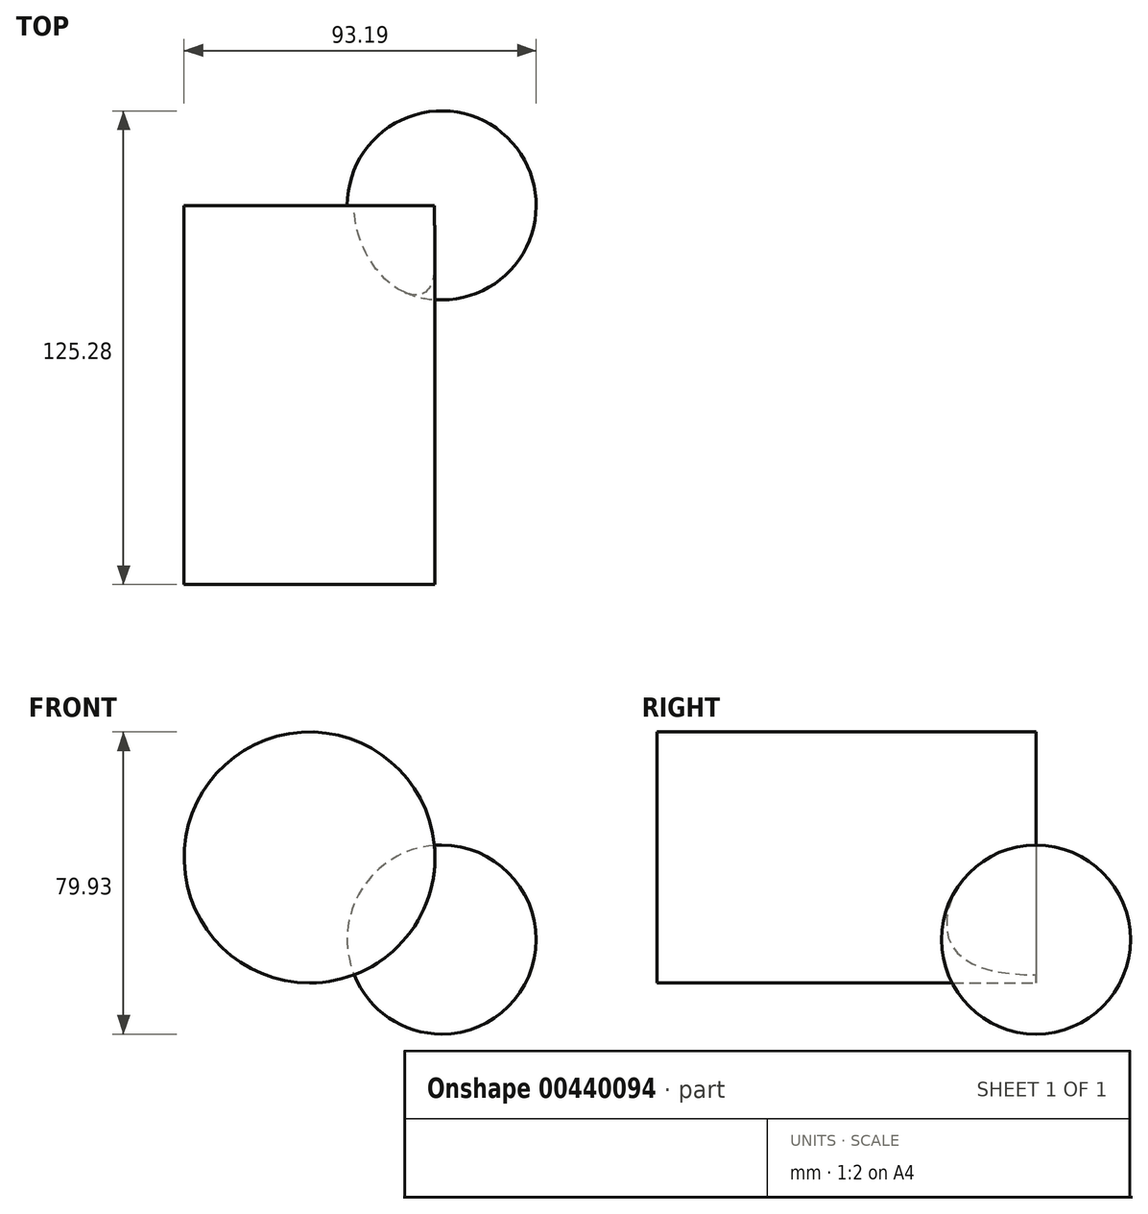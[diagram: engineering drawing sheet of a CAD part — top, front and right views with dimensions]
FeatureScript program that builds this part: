
annotation { "Feature Type Name" : "Feature", "Feature Type Description" : "" }
export const myFeature = defineFeature(function(context is Context, id is Id, definition is map)
    precondition{}
    {
        {
            var Q0;
            Q0=qCreatedBy(makeId("Front.planeOp"),FACE);
            var sketch = newSketch(context, id + "F0", { "sketchPlane" : qUnion([Q0])});
            skLineSegment(sketch, "E0", {"start": v(0, 0) * mm, "end": v(0, 50) * mm});
            skArc(sketch, "E1", {"start": v(0, 0) * mm, "mid": v(25, 25) * mm, "end": v(0, 50) * mm});
            skLineSegment(sketch, "E2", {"start": v(0, 50) * mm, "end": v(0, 76.97) * mm, "construction": true});
            skSolve(sketch);
        }
        {
            var Q0;
            Q0=makeQuery(id+"F0.imprint","IMPRINT",FACE,{"disambiguationData":[TD([[makeQuery(id+"F0.imprint","IMPRINT",EDGE,{"derivedFrom":sQuery(id+"F0.wireOp",EDGE,"E0")}),-1.0]])]});
            var Q1;
            Q1=sQuery(id+"F0.wireOp",EDGE,"E0");
            revolve(context, id + "F1", {"entities" : qUnion([Q0]), "axis" : qUnion([Q1]), "revolveType" : RevolveType.FULL});
        }
        {
            var Q0;
            Q0=qCreatedBy(makeId("Front.planeOp"),FACE);
            var sketch = newSketch(context, id + "F2", { "sketchPlane" : qUnion([Q0])});
            skCircle(sketch, "E3", {"center": v(-34.98, 46.72) * mm, "radius": 33.2 * mm});
            skSolve(sketch);
        }
        {
            var Q0;
            Q0 = qSketchRegion(id + "F2", true);
            extrude(context, id + "F3", {"entities" : qUnion([Q0]), "operationType" : NewBodyOperationType.ADD, "depth" : 100.28 * mm});
        }
    });
